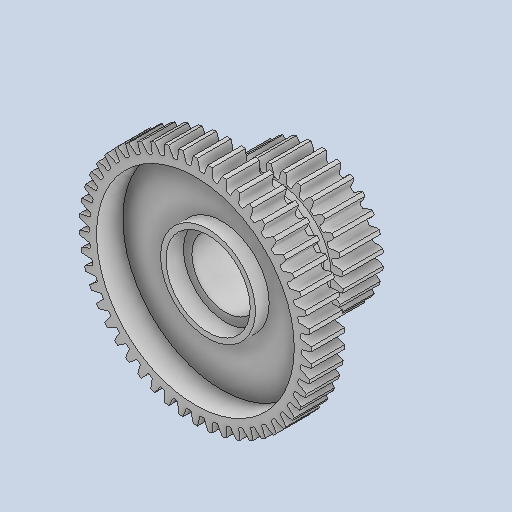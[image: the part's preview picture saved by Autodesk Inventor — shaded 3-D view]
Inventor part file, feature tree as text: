
AUTODESK INVENTOR PART (.ipt)
format: ipt  version: 2022.3 (Build 263350000, 350)  size: 768,512 bytes
history: native  units: in
note: dims shown in document units (in); Inventor stores cm internally (conversion verified against a paired STEP export)
features: chamfer x1
ambient origin geometry x8: Origin, YZ Plane, XZ Plane, XY Plane, X Axis, Y Axis, Z Axis, Center Point
bodies: Solid1 (feature_tree)
feature tree (1):
  chamfer  "Chamfer1"  [1 undecoded]
note: 1 required parameter value undecoded (feature->parameter linkage not recoverable at this tier; creation-order binding heuristic only, values carry confidence <= 0.55)
